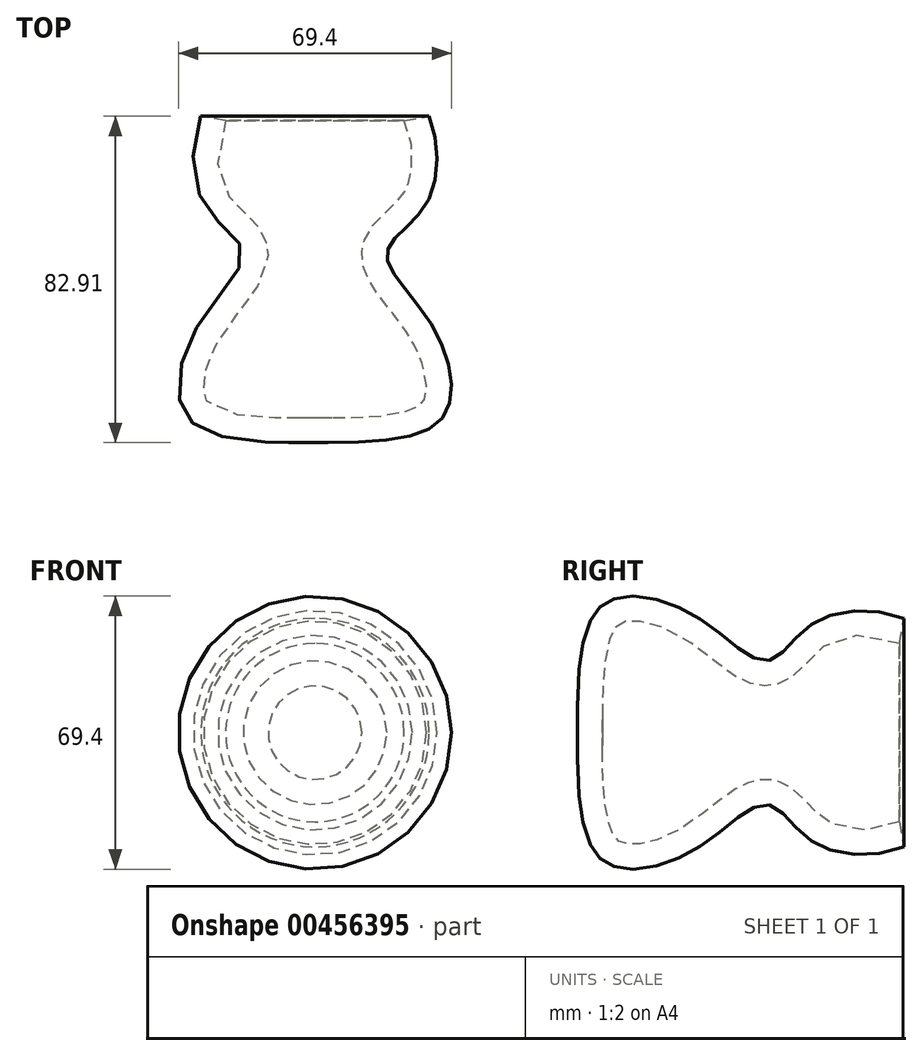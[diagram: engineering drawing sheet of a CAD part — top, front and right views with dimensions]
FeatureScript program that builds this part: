
annotation { "Feature Type Name" : "Feature", "Feature Type Description" : "" }
export const myFeature = defineFeature(function(context is Context, id is Id, definition is map)
    precondition{}
    {
        {
            var Q0;
            Q0=qCreatedBy(makeId("Top.planeOp"),FACE);
            var sketch = newSketch(context, id + "F0", { "sketchPlane" : qUnion([Q0])});
            skLineSegment(sketch, "E0", {"start": v(0, 75.74) * mm, "end": v(0, -75.74) * mm});
            skFitSpline(sketch, "E1", {"points": [v(-12.8, -54.71) * mm, v(32.3, -48.62) * mm, v(29.57, -24.84) * mm, v(18.29, -6.55) * mm, v(28.35, 5.94) * mm, v(26.52, 32.77) * mm], "startDerivative": vector(229.21, 0) * mm, "endDerivative": vector(-76.34, 107.78) * mm});
            skFitSpline(sketch, "E2.0", {"points": [v(-12.8, -48.36) * mm, v(-10.38, -48.36) * mm, v(-5.6, -48.4) * mm, v(1.23, -48.48) * mm, v(7.63, -48.47) * mm, v(13.43, -48.28) * mm, v(18.5, -47.83) * mm, v(21.94, -47.19) * mm, v(24.1, -46.55) * mm, v(25.4, -46.03) * mm, v(26.21, -45.58) * mm, v(26.7, -45.25) * mm, v(27, -45.01) * mm, v(27.19, -44.83) * mm, v(27.31, -44.7) * mm, v(27.43, -44.56) * mm, v(27.55, -44.38) * mm, v(27.75, -44.05) * mm, v(27.98, -43.53) * mm, v(28.21, -42.68) * mm, v(28.35, -41.6) * mm, v(28.36, -39.88) * mm, v(28.02, -37.3) * mm, v(27.16, -34.42) * mm, v(26.2, -32.05) * mm, v(25.36, -30.28) * mm, v(24.56, -28.84) * mm, v(23.88, -27.72) * mm, v(23.16, -26.6) * mm, v(22.18, -25.18) * mm, v(20.5, -22.94) * mm, v(18.73, -20.7) * mm, v(16.98, -18.47) * mm, v(15.71, -16.77) * mm, v(14.52, -15) * mm, v(13.6, -13.42) * mm, v(12.96, -12.04) * mm, v(12.54, -10.92) * mm, v(12.19, -9.7) * mm, v(12, -8.6) * mm, v(11.91, -7.67) * mm, v(11.9, -6.95) * mm, v(11.93, -6.2) * mm, v(12.02, -5.44) * mm, v(12.17, -4.7) * mm, v(12.42, -3.77) * mm, v(12.83, -2.7) * mm, v(13.42, -1.56) * mm, v(14.27, -0.23) * mm, v(15.4, 1.15) * mm, v(16.73, 2.53) * mm, v(18.03, 3.75) * mm, v(19.26, 4.9) * mm, v(20.39, 6) * mm, v(21.21, 6.88) * mm, v(21.8, 7.58) * mm, v(22.2, 8.1) * mm, v(22.49, 8.53) * mm, v(22.7, 8.87) * mm, v(22.85, 9.13) * mm, v(23, 9.39) * mm, v(23.19, 9.76) * mm, v(23.4, 10.25) * mm, v(23.66, 10.88) * mm, v(23.96, 11.79) * mm, v(24.28, 13.02) * mm, v(24.54, 14.63) * mm, v(24.73, 16.89) * mm, v(24.63, 19.86) * mm, v(23.98, 23.39) * mm, v(22.86, 26.6) * mm, v(21.87, 28.35) * mm, v(21.34, 29.1) * mm]});
            skLineSegment(sketch, "E3", {"start": v(22.58, 26.98) * mm, "end": v(29.02, 28.1) * mm});
            skSolve(sketch);
        }
        {
            var Q0;
            {var subQ0=sQuery(id+"F0.wireOp",EDGE,"E1");Q0=makeQuery(id+"F0.imprint","IMPRINT",FACE,{"disambiguationData":[TD([[makeQuery(id+"F0.imprint","IMPRINT",EDGE,{"derivedFrom":subQ0}),1.0]])]});}
            var Q1;
            Q1=sQuery(id+"F0.wireOp",EDGE,"E0");
            revolve(context, id + "F1", {"entities" : qUnion([Q0]), "axis" : qUnion([Q1]), "revolveType" : RevolveType.FULL});
        }
    });
